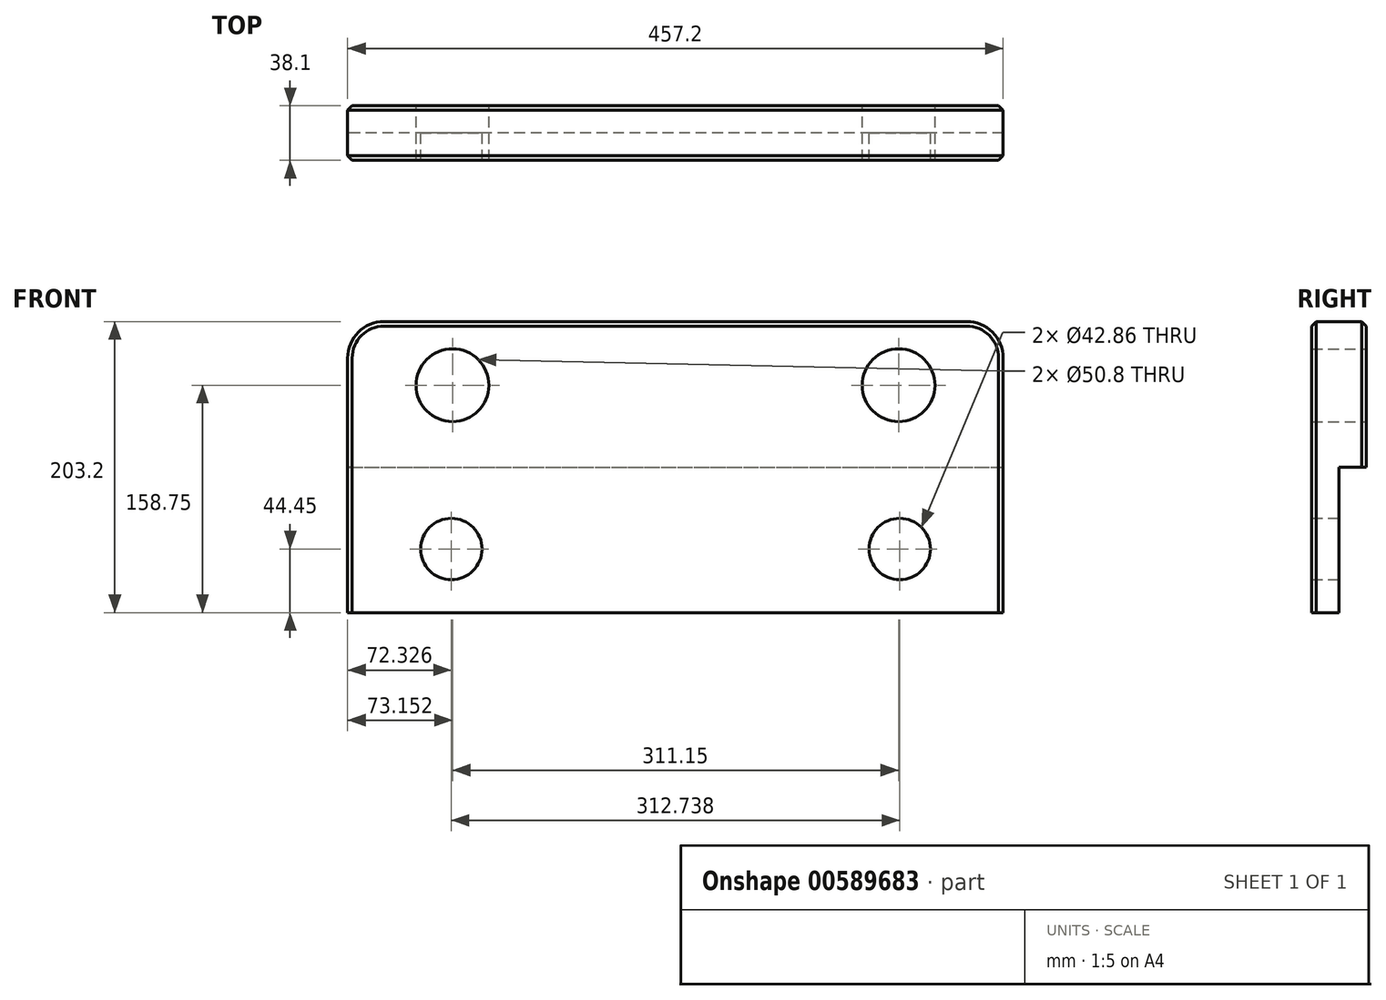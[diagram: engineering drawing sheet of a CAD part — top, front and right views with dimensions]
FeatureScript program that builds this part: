
annotation { "Feature Type Name" : "Feature", "Feature Type Description" : "" }
export const myFeature = defineFeature(function(context is Context, id is Id, definition is map)
    precondition{}
    {
        {
            var Q0;
            Q0=qCreatedBy(makeId("Front.planeOp"),FACE);
            var sketch = newSketch(context, id + "F0", { "sketchPlane" : qUnion([Q0])});
            skLineSegment(sketch, "E0.bottom", {"start": v(203.2, 101.6) * mm, "end": v(-203.2, 101.6) * mm});
            skLineSegment(sketch, "E0.top", {"start": v(228.6, -101.6) * mm, "end": v(-228.6, -101.6) * mm});
            skLineSegment(sketch, "E0.left", {"start": v(228.6, 76.2) * mm, "end": v(228.6, -101.6) * mm});
            skLineSegment(sketch, "E0.right", {"start": v(-228.6, 76.2) * mm, "end": v(-228.6, -101.6) * mm});
            skPoint(sketch, "E0.middle", {"position": v(0, 0) * mm});
            skLineSegment(sketch, "E1", {"start": v(-228.6, 0) * mm, "end": v(228.6, 0) * mm});
            skCircle(sketch, "E2", {"center": v(-155.45, 57.15) * mm, "radius": 25.4 * mm});
            skCircle(sketch, "E3", {"center": v(-156.27, -57.15) * mm, "radius": 21.43 * mm});
            skCircle(sketch, "E4", {"center": v(155.7, 57.15) * mm, "radius": 25.4 * mm});
            skCircle(sketch, "E5", {"center": v(156.46, -57.15) * mm, "radius": 21.43 * mm});
            skPoint(sketch, "E6.visualSharp", {"position": v(-228.6, 101.6) * mm});
            skArc(sketch, "E6.filletArc", {"start": v(-203.2, 101.6) * mm, "mid": v(-221.16, 94.16) * mm, "end": v(-228.6, 76.2) * mm});
            skPoint(sketch, "E7.visualSharp", {"position": v(228.6, 101.6) * mm});
            skArc(sketch, "E7.filletArc", {"start": v(228.6, 76.2) * mm, "mid": v(221.16, 94.16) * mm, "end": v(203.2, 101.6) * mm});
            skSolve(sketch);
        }
        {
            var Q0;
            Q0 = qSketchRegion(id + "F0", true);
            extrude(context, id + "F1", {"entities" : qUnion([Q0]), "depth" : 19.05 * mm, "offsetDistance" : 25.4 * mm});
        }
        {
            var Q0;
            {var subQ2=sQuery(id+"F0.wireOp",EDGE,"E0.bottom");Q0=makeQuery(id+"F0.imprint","IMPRINT",FACE,{"disambiguationData":[TD([[makeQuery(id+"F0.imprint","IMPRINT",EDGE,{"derivedFrom":subQ2}),1.0]])]});}
            extrude(context, id + "F2", {"entities" : qUnion([Q0]), "operationType" : NewBodyOperationType.ADD, "oppositeDirection" : true, "depth" : 19.05 * mm, "offsetDistance" : 25.4 * mm});
        }
        {
            var Q0;
            {var subQ0=sQuery(id+"F0.wireOp",EDGE,"E6.filletArc");var subQ1=sQuery(id+"F0.wireOp",EDGE,"E0.bottom");Q0=makeQuery(id+"F2.boolean.opBoolean","MERGE",EDGE,{"derivedFrom":[makeQuery(id+"F1.opExtrude","SWEPT_EDGE",EDGE,{"disambiguationData":[OSD([subQ1,subQ0])]}),makeQuery(id+"F2.opExtrude","SWEPT_EDGE",EDGE,{"disambiguationData":[OSD([subQ1,subQ0])]})]});}
            var Q1;
            Q1=makeQuery(id+"F1.opExtrude","CAP_EDGE",EDGE,{"disambiguationData":[OSD([sQuery(id+"F0.wireOp",EDGE,"E0.right")])],"isStart":false});
            var Q2;
            Q2=makeQuery(id+"F2.opExtrude","CAP_EDGE",EDGE,{"disambiguationData":[OSD([sQuery(id+"F0.wireOp",EDGE,"E0.right")])],"isStart":false});
            chamfer(context, id + "F3", {"entities" : qUnion([Q0, Q1, Q2]), "width" : 3.17 * mm, "tangentPropagation" : true});
        }
    });
